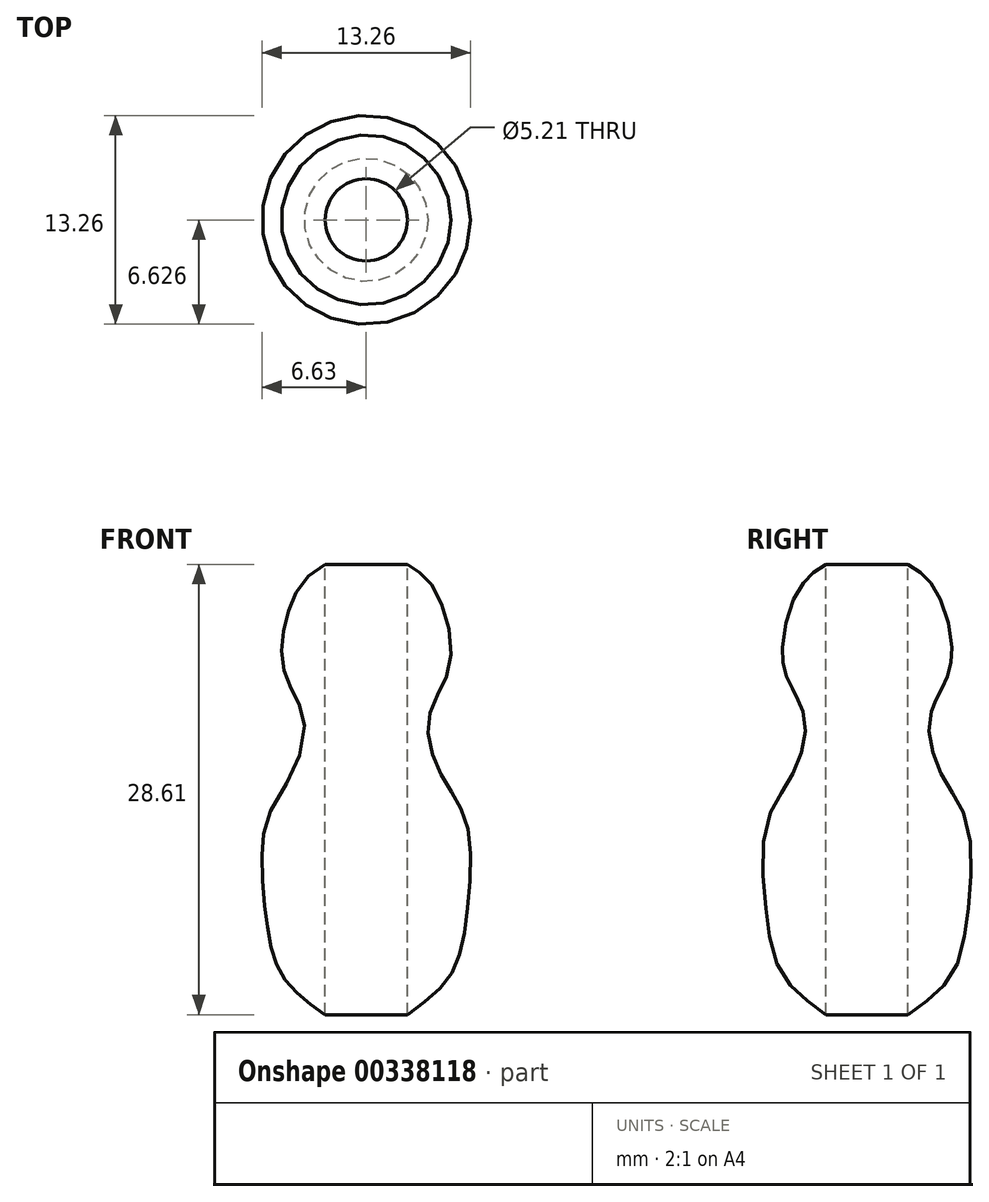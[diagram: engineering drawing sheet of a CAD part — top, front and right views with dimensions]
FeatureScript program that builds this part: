
annotation { "Feature Type Name" : "Feature", "Feature Type Description" : "" }
export const myFeature = defineFeature(function(context is Context, id is Id, definition is map)
    precondition{}
    {
        {
            var Q0;
            Q0=qCreatedBy(makeId("Right.planeOp"),FACE);
            var sketch = newSketch(context, id + "F0", { "sketchPlane" : qUnion([Q0])});
            skFitSpline(sketch, "E0", {"points": [v(0, 0) * mm, v(-2.7, 2.44) * mm, v(-3.77, 6.3) * mm, v(-3.77, 12.14) * mm, v(-2.18, 15.2) * mm, v(-1.38, 18.91) * mm, v(-2.7, 22.23) * mm, v(-1.64, 27.15) * mm, v(0, 28.6) * mm], "startDerivative": vector(-25.7, 18.22) * mm, "endDerivative": vector(18.23, 10.87) * mm});
            skLineSegment(sketch, "E1", {"start": v(0, 28.6) * mm, "end": v(0, 0) * mm});
            skLineSegment(sketch, "E2", {"start": v(2.6, 28.6) * mm, "end": v(2.6, 0) * mm});
            skSolve(sketch);
        }
        {
            var Q0;
            Q0=makeQuery(id+"F0.imprint","IMPRINT",FACE,{"disambiguationData":[TD([[makeQuery(id+"F0.imprint","IMPRINT",EDGE,{"derivedFrom":sQuery(id+"F0.wireOp",EDGE,"E0")}),-1.0]])]});
            var Q1;
            Q1=sQuery(id+"F0.wireOp",EDGE,"E2");
            revolve(context, id + "F1", {"entities" : qUnion([Q0]), "axis" : qUnion([Q1]), "revolveType" : RevolveType.FULL});
        }
    });
